# Revit family: Kühltische GN1-1 - Eigen
name_source: partatom
category: Sonderausstattung
revit_build: Autodesk Revit 2015 (Build: 20160512_1515(x64)
units: mm (PartAtom-declared; Revit-internal decimal feet)

## types (1)
- Kühltische GN1-1 - Eigen
    Abstand Display seitlich = 60 mm  [stored 0.19685 ft]
    Abstand Logo = 320 mm  [stored 1.04987 ft]
    Artnr mit Platte = KTM 711172-76
    Artnr mit Platte und Aufkantung = KTM 711171-76
    Artnr ohne Platte = KTM 711170-76
    Aufkantung Höhe = 50 mm  [stored 0.164042 ft]
    Aufkantung Stärke = 6 mm  [stored 0.019685 ft]
    Breite = 790 mm  [stored 2.59186 ft]
    Energieverbrauch = 2,6 kWh/24 h
    Höhe Elektroanschluss = 150 mm
    Kapazität = 1 x 11 x GN1/1
    Korpus Breite = 445 mm  [stored 1.45997 ft]
    Korpus Höhe = 760 mm  [stored 2.49344 ft]
    Korpus Tiefe = 620 mm
    Kälteleistung = 380 Watt -15°C VT/+32°C UT
    Kältemittel = R290
    Material = Edelstahl AISI 304
    Pfosten 1 = Nein
    Pfosten 2 = Nein
    Pfosten 3 = Nein
    Pfosten Abstand = 400 mm  [stored 1.31234 ft]
    Pfosten Anzahl = 0
    Pfosten Breite = 100 mm  [stored 0.328084 ft]
    Pfosten Tiefe = 50 mm  [stored 0.164042 ft]
    Platte Stärke = 50 mm  [stored 0.164042 ft]
    Platte Tiefe = 700 mm  [stored 2.29659 ft]
    Pole = 1
    Rückwand Stärke = 50 mm  [stored 0.164042 ft]
    Scheinleistung = 0 VA
    Seitenteil Breite = 330 mm
    Seitenteilwand Stärke = 15 mm  [stored 0.0492126 ft]
    Seitenwand Stärke = 50 mm  [stored 0.164042 ft]
    Sockelhöhe = 150 mm
    Spannung = 230 V
    Temp. Bereich = -2°C bis +10°C
    Tür_1 = Ja
    Tür_2 = Nein
    Tür_3 = Nein
    Tür_4 = Nein
    Türen Anzahl = 1
    Türen Breite = 390 mm  [stored 1.27953 ft]
    Türen Breite halb = 195 mm  [stored 0.639764 ft]
    Türen Höhe = 740 mm  [stored 2.42782 ft]
    Türen Lücke = 20 mm  [stored 0.0656168 ft]
    Türen Stärke = 50 mm  [stored 0.164042 ft]
    Versatz Tür zu Seitenteil = 40 mm  [stored 0.131234 ft]
    Wand oben Stärke = 50 mm  [stored 0.164042 ft]
    Wand unten Stärke = 50 mm  [stored 0.164042 ft]
    Watt = 440 W
    Öffnungstiefe = 470 mm  [stored 1.54199 ft]

note: [stored X ft] marks values corroborated as IEEE doubles in the binary element streams (Revit-internal decimal feet)

## geometry (parser evidence)
native form markers: Blend x14, Sweep x2
no freeform markers — native parametric forms only
